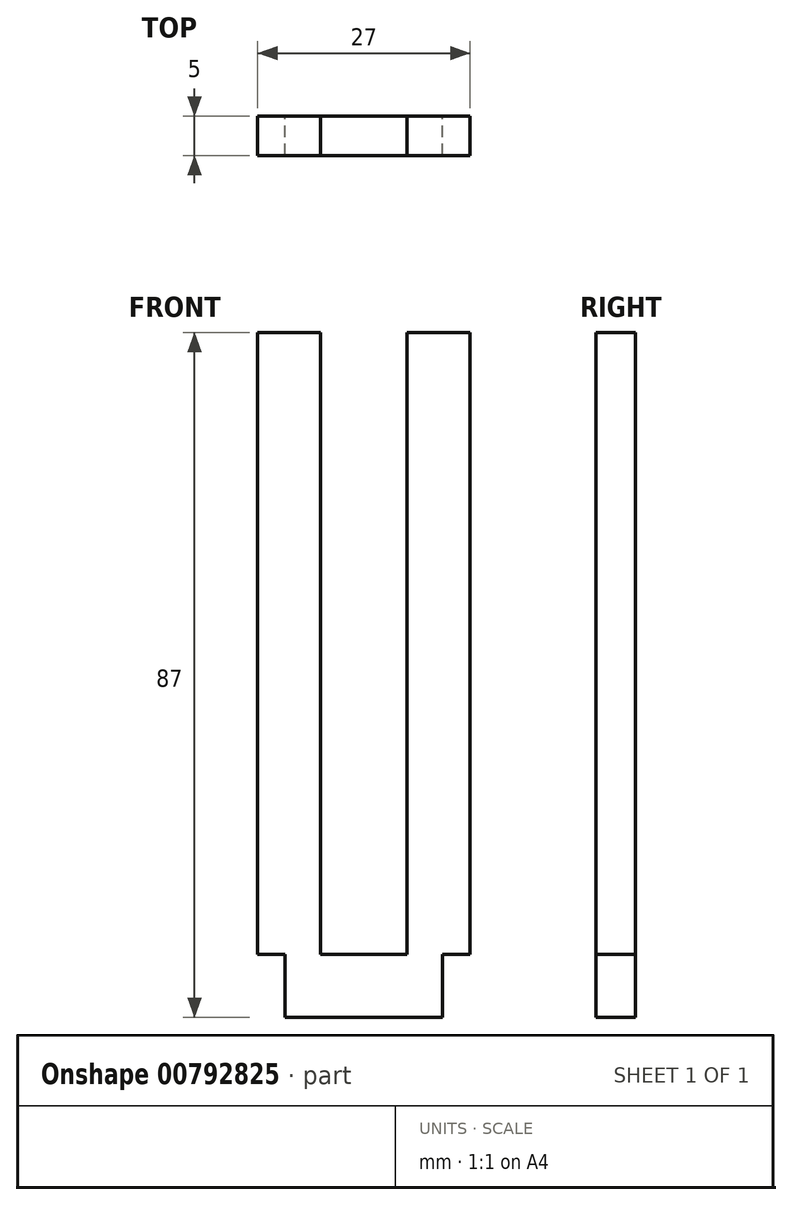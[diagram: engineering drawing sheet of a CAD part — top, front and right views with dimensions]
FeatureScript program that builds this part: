
annotation { "Feature Type Name" : "Feature", "Feature Type Description" : "" }
export const myFeature = defineFeature(function(context is Context, id is Id, definition is map)
    precondition{}
    {
        {
            var Q0;
            Q0=qCreatedBy(makeId("Front.planeOp"), FACE);
            var sketch = newSketch(context, id + "F0", { "sketchPlane" : qUnion([Q0])});
            skLineSegment(sketch, "E0", {"start": v(0, 55.52) * mm, "end": v(0, -73.42) * mm, "construction": true});
            skLineSegment(sketch, "E1", {"start": v(61.74, 0) * mm, "end": v(-48.7, 0) * mm, "construction": true});
            skPoint(sketch, "E2.middle", {"position": v(0, 0) * mm});
            skLineSegment(sketch, "E3", {"start": v(-5.5, 29) * mm, "end": v(-5.5, 66) * mm});
            skLineSegment(sketch, "E4.MirrorCS", {"start": v(5.5, 29) * mm, "end": v(5.5, 66) * mm});
            skLineSegment(sketch, "E5", {"start": v(-13.5, 66) * mm, "end": v(-5.5, 66) * mm});
            skLineSegment(sketch, "E6", {"start": v(10, -21) * mm, "end": v(10, -13) * mm});
            skLineSegment(sketch, "E7", {"start": v(10, -13) * mm, "end": v(13.5, -13) * mm});
            skLineSegment(sketch, "E8", {"start": v(13.5, 21) * mm, "end": v(13.5, -13) * mm});
            skLineSegment(sketch, "E9.MirrorCS", {"start": v(-13.5, 21) * mm, "end": v(-13.5, -13) * mm});
            skLineSegment(sketch, "E10.MirrorCS", {"start": v(-10, -21) * mm, "end": v(-10, -13) * mm});
            skLineSegment(sketch, "E11.MirrorCS", {"start": v(-10, -13) * mm, "end": v(-13.5, -13) * mm});
            skLineSegment(sketch, "E12", {"start": v(-10, -21) * mm, "end": v(10, -21) * mm});
            skLineSegment(sketch, "E13", {"start": v(-13.5, 66) * mm, "end": v(-13.5, 21) * mm});
            skLineSegment(sketch, "E14", {"start": v(13.5, 21) * mm, "end": v(13.5, 66) * mm});
            skLineSegment(sketch, "E15", {"start": v(13.5, 66) * mm, "end": v(5.5, 66) * mm});
            skLineSegment(sketch, "E16", {"start": v(-5.5, -13) * mm, "end": v(5.5, -13) * mm});
            skLineSegment(sketch, "E17", {"start": v(-5.5, -13) * mm, "end": v(-5.5, 29) * mm});
            skLineSegment(sketch, "E18", {"start": v(5.5, 29) * mm, "end": v(5.5, -13) * mm});
            skSolve(sketch);
        }
        {
            var Q0;
            Q0 = qSketchRegion(id + "F0", true);
            extrude(context, id + "F1", {"entities" : qUnion([Q0]), "depth" : 5 * mm, "offsetDistance" : 25 * mm});
        }
    });
